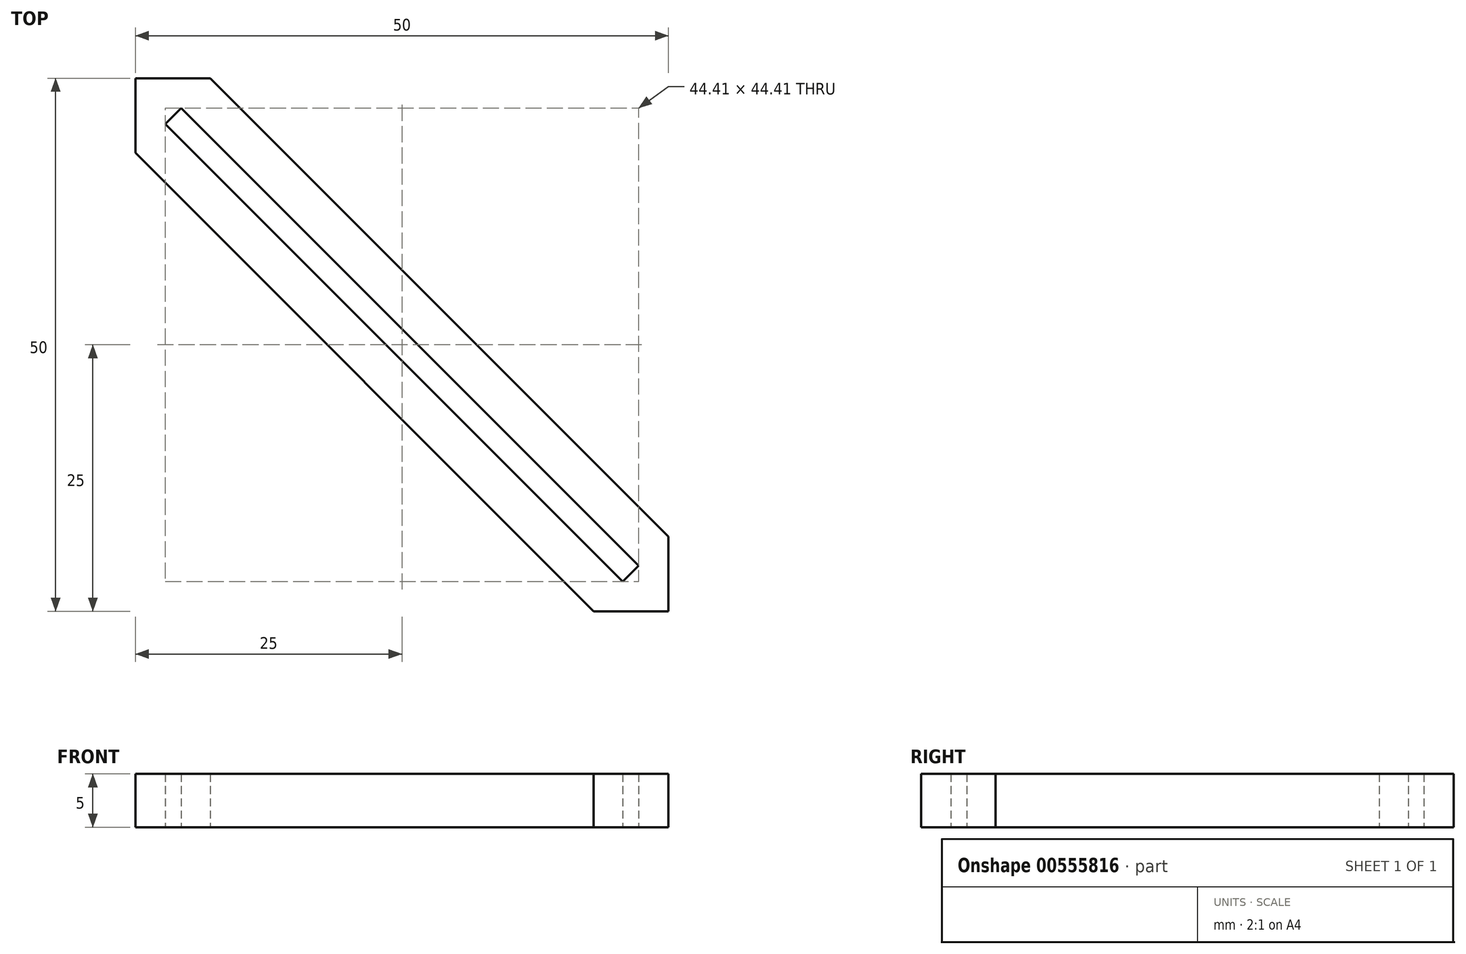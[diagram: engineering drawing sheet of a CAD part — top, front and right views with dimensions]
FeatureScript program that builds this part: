
annotation { "Feature Type Name" : "Feature", "Feature Type Description" : "" }
export const myFeature = defineFeature(function(context is Context, id is Id, definition is map)
    precondition{}
    {
        {
            var Q0;
            Q0=qCreatedBy(makeId("Top.planeOp"),FACE);
            var sketch = newSketch(context, id + "F0", { "sketchPlane" : qUnion([Q0])});
            skLineSegment(sketch, "E0", {"start": v(-50, 43) * mm, "end": v(-7, 0) * mm});
            skLineSegment(sketch, "E1", {"start": v(-43, 50) * mm, "end": v(-50, 50) * mm});
            skLineSegment(sketch, "E2", {"start": v(-50, 43) * mm, "end": v(-50, 50) * mm});
            skLineSegment(sketch, "E3", {"start": v(-7, 0) * mm, "end": v(0, 0) * mm});
            skLineSegment(sketch, "E4", {"start": v(0, 0) * mm, "end": v(0, 7) * mm});
            skLineSegment(sketch, "E5", {"start": v(0, 7) * mm, "end": v(-43, 50) * mm});
            skLineSegment(sketch, "E6.bottom", {"start": v(-45.72, 47.2) * mm, "end": v(-2.8, 4.28) * mm});
            skLineSegment(sketch, "E6.top", {"start": v(-47.2, 45.72) * mm, "end": v(-4.28, 2.8) * mm});
            skLineSegment(sketch, "E6.left", {"start": v(-45.72, 47.2) * mm, "end": v(-47.2, 45.72) * mm});
            skLineSegment(sketch, "E6.right", {"start": v(-2.8, 4.28) * mm, "end": v(-4.28, 2.8) * mm});
            skSolve(sketch);
        }
        {
            var Q0;
            Q0=makeQuery(id+"F0.imprint","IMPRINT",FACE,{"disambiguationData":[TD([[makeQuery(id+"F0.imprint","IMPRINT",EDGE,{"derivedFrom":sQuery(id+"F0.wireOp",EDGE,"E0")}),1.0]])]});
            extrude(context, id + "F1", {"entities" : qUnion([Q0]), "depth" : 5 * mm, "offsetDistance" : 25 * mm});
        }
    });
